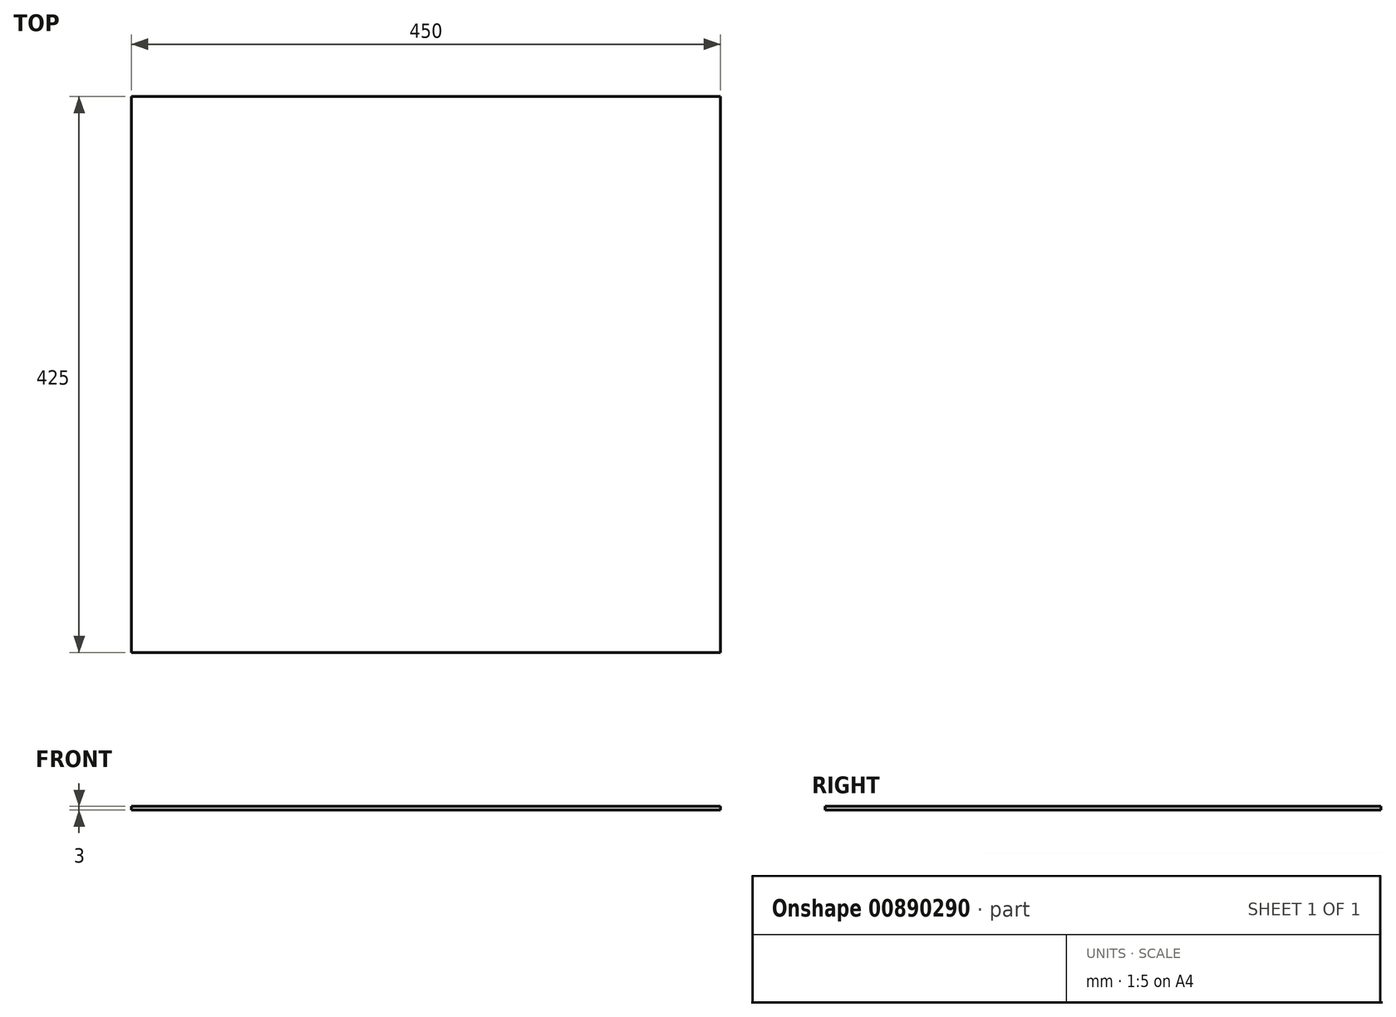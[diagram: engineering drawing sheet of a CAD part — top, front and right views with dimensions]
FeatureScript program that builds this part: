
annotation { "Feature Type Name" : "Feature", "Feature Type Description" : "" }
export const myFeature = defineFeature(function(context is Context, id is Id, definition is map)
    precondition{}
    {
        {
            var Q0;
            Q0=qCreatedBy(makeId("Top.planeOp"),FACE);
            var sketch = newSketch(context, id + "F0", { "sketchPlane" : qUnion([Q0])});
            skLineSegment(sketch, "E0.bottom", {"start": v(225, -212.5) * mm, "end": v(-225, -212.5) * mm});
            skLineSegment(sketch, "E0.top", {"start": v(225, 212.5) * mm, "end": v(-225, 212.5) * mm});
            skLineSegment(sketch, "E0.left", {"start": v(225, -212.5) * mm, "end": v(225, 212.5) * mm});
            skLineSegment(sketch, "E0.right", {"start": v(-225, -212.5) * mm, "end": v(-225, 212.5) * mm});
            skPoint(sketch, "E0.middle", {"position": v(0, 0) * mm});
            skSolve(sketch);
        }
        {
            var Q0;
            Q0=qSketchRegion(id+"F0",true);
            extrude(context, id + "F1", {"entities" : qUnion([Q0]), "depth" : 3 * mm, "offsetDistance" : 25 * mm});
        }
    });
